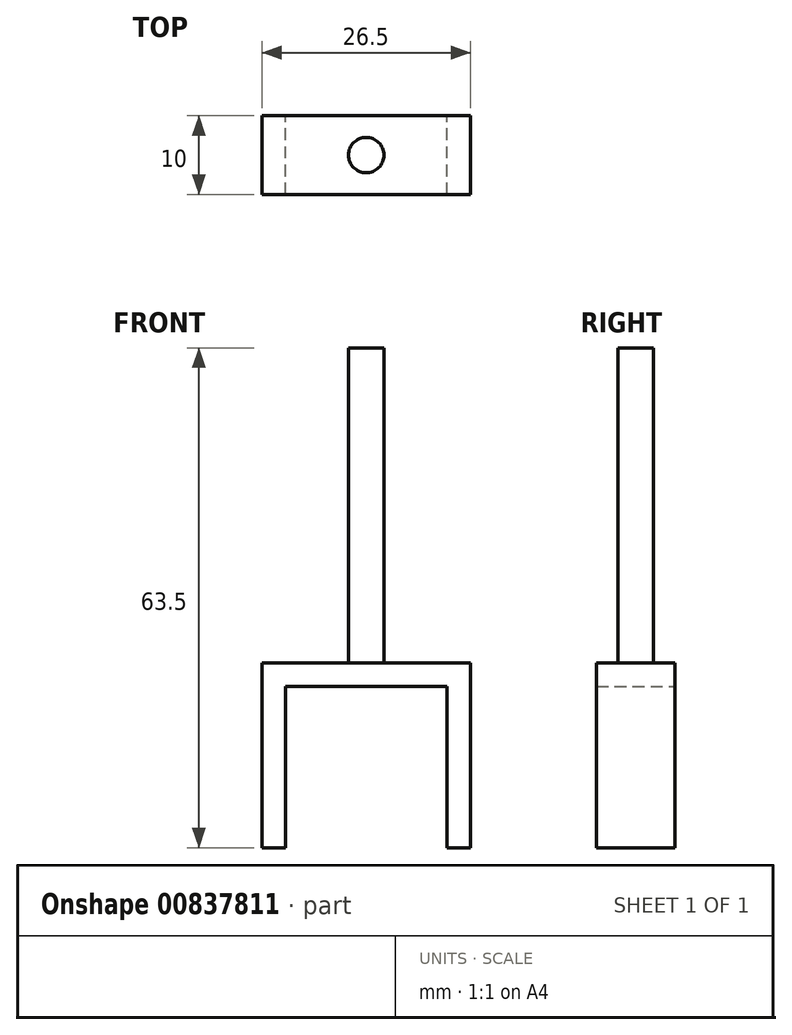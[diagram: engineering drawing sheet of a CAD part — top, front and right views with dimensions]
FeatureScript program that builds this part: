
annotation { "Feature Type Name" : "Feature", "Feature Type Description" : "" }
export const myFeature = defineFeature(function(context is Context, id is Id, definition is map)
    precondition{}
    {
        {
            var Q0;
            Q0=qCreatedBy(makeId("Front.planeOp"),FACE);
            var sketch = newSketch(context, id + "F0", { "sketchPlane" : qUnion([Q0])});
            skLineSegment(sketch, "E0.bottom", {"start": v(-14.14, -6.33) * mm, "end": v(6.36, -6.33) * mm});
            skLineSegment(sketch, "E0.top", {"start": v(-14.14, 14.17) * mm, "end": v(6.36, 14.17) * mm});
            skLineSegment(sketch, "E0.left", {"start": v(-14.14, -6.33) * mm, "end": v(-14.14, 14.17) * mm});
            skLineSegment(sketch, "E0.right", {"start": v(6.36, -6.33) * mm, "end": v(6.36, 14.17) * mm});
            skLineSegment(sketch, "E1.bottom", {"start": v(-14.14, -6.33) * mm, "end": v(-17.14, -6.33) * mm});
            skLineSegment(sketch, "E1.top", {"start": v(-14.14, 17.17) * mm, "end": v(-17.14, 17.17) * mm});
            skLineSegment(sketch, "E1.left", {"start": v(-14.14, -6.33) * mm, "end": v(-14.14, 17.17) * mm});
            skLineSegment(sketch, "E1.right", {"start": v(-17.14, -6.33) * mm, "end": v(-17.14, 17.17) * mm});
            skPoint(sketch, "E2.oppositeSnap0", {"position": v(-15.64, 17.17) * mm});
            skLineSegment(sketch, "E2.bottom", {"start": v(6.36, -6.33) * mm, "end": v(9.36, -6.33) * mm});
            skLineSegment(sketch, "E2.top", {"start": v(6.36, 17.17) * mm, "end": v(9.36, 17.17) * mm});
            skLineSegment(sketch, "E2.left", {"start": v(6.36, -6.33) * mm, "end": v(6.36, 17.17) * mm});
            skLineSegment(sketch, "E2.right", {"start": v(9.36, -6.33) * mm, "end": v(9.36, 17.17) * mm});
            skLineSegment(sketch, "E3.bottom", {"start": v(6.36, 17.17) * mm, "end": v(-14.14, 17.17) * mm});
            skLineSegment(sketch, "E3.top", {"start": v(6.36, 14.17) * mm, "end": v(-14.14, 14.17) * mm});
            skLineSegment(sketch, "E3.left", {"start": v(6.36, 17.17) * mm, "end": v(6.36, 14.17) * mm});
            skLineSegment(sketch, "E3.right", {"start": v(-14.14, 17.17) * mm, "end": v(-14.14, 14.17) * mm});
            skSolve(sketch);
        }
        {
            var Q0;
            Q0=makeQuery(id+"F0.imprint","IMPRINT",FACE,{"disambiguationData":[TD([[makeQuery(id+"F0.imprint","IMPRINT",EDGE,{"derivedFrom":sQuery(id+"F0.wireOp",EDGE,"E1.bottom")}),-1.0]])]});
            var Q1;
            Q1=makeQuery(id+"F0.imprint","IMPRINT",FACE,{"disambiguationData":[TD([[makeQuery(id+"F0.imprint","IMPRINT",EDGE,{"derivedFrom":sQuery(id+"F0.wireOp",EDGE,"E3.bottom")}),1.0]])]});
            var Q2;
            Q2=makeQuery(id+"F0.imprint","IMPRINT",FACE,{"disambiguationData":[TD([[makeQuery(id+"F0.imprint","IMPRINT",EDGE,{"derivedFrom":sQuery(id+"F0.wireOp",EDGE,"E2.bottom")}),1.0]])]});
            extrude(context, id + "F1", {"entities" : qUnion([Q0, Q1, Q2]), "depth" : 10 * mm, "offsetDistance" : 25 * mm});
        }
        {
            var Q0;
            Q0=makeQuery(id+"F1.opExtrude","SWEPT_FACE",FACE,{"disambiguationData":[OSD([sQuery(id+"F0.wireOp",EDGE,"E1.top"),sQuery(id+"F0.wireOp",EDGE,"E2.top"),sQuery(id+"F0.wireOp",EDGE,"E3.bottom")])]});
            var sketch = newSketch(context, id + "F2", { "sketchPlane" : qUnion([Q0])});
            skCircle(sketch, "E4", {"center": v(-3.89, -5) * mm, "radius": 2.25 * mm});
            skPoint(sketch, "E4.centerSnap0", {"position": v(-3.89, 0) * mm});
            skPoint(sketch, "E5", {"position": v(-17.14, -5) * mm});
            skSolve(sketch);
        }
        {
            var Q0;
            Q0=makeQuery(id+"F2.imprint","IMPRINT",FACE,{"disambiguationData":[TD([[makeQuery(id+"F2.imprint","IMPRINT",EDGE,{"derivedFrom":sQuery(id+"F2.wireOp",EDGE,"E4")}),1.0]])]});
            extrude(context, id + "F3", {"entities" : qUnion([Q0]), "operationType" : NewBodyOperationType.ADD, "depth" : 40 * mm, "offsetDistance" : 25 * mm});
        }
    });
